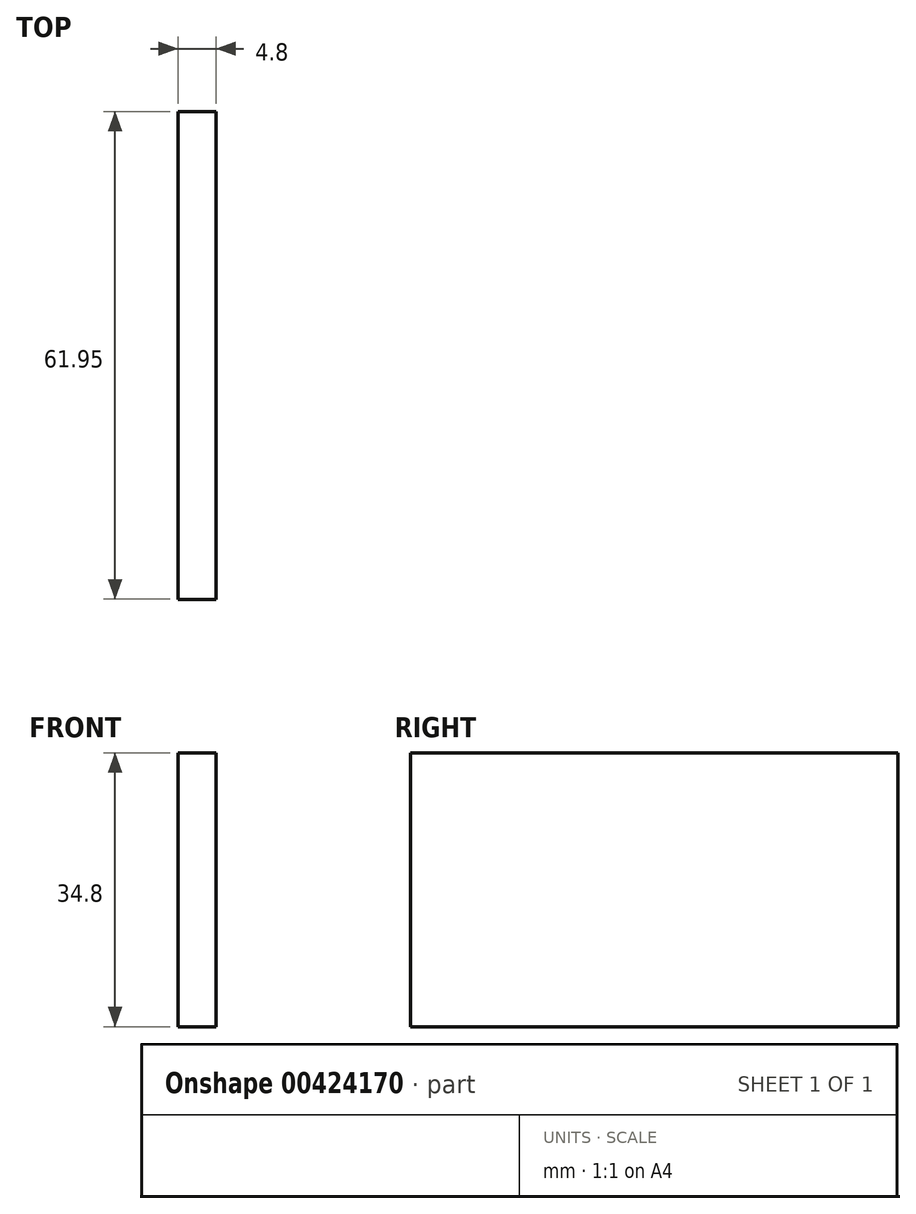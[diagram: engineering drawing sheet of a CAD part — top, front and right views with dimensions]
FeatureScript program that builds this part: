
annotation { "Feature Type Name" : "Feature", "Feature Type Description" : "" }
export const myFeature = defineFeature(function(context is Context, id is Id, definition is map)
    precondition{}
    {
        {
            var Q0;
            Q0=qCreatedBy(makeId("Top.planeOp"),FACE);
            var sketch = newSketch(context, id + "F0", { "sketchPlane" : qUnion([Q0])});
            skLineSegment(sketch, "E0.bottom", {"start": v(-4.8, 32.85) * mm, "end": v(0, 32.85) * mm});
            skLineSegment(sketch, "E0.top", {"start": v(-4.8, -29.1) * mm, "end": v(0, -29.1) * mm});
            skLineSegment(sketch, "E0.left", {"start": v(-4.8, 32.85) * mm, "end": v(-4.8, -29.1) * mm});
            skLineSegment(sketch, "E0.right", {"start": v(0, 32.85) * mm, "end": v(0, -29.1) * mm});
            skSolve(sketch);
        }
        {
            var Q0;
            Q0 = qSketchRegion(id + "F0", true);
            extrude(context, id + "F1", {"entities" : qUnion([Q0]), "depth" : 34.8 * mm});
        }
    });
